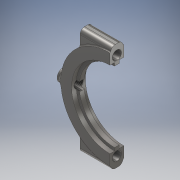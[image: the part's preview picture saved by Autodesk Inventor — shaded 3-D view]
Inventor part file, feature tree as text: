
AUTODESK INVENTOR PART (.ipt)
format: ipt  version: 2017 (Build 210142000, 142)  size: 296,960 bytes
history: native  units: mm
features: extrude x6, sketch x3, fillet x2, plane x2, thread x1, projected_geometry x1
ambient origin geometry x8: Origin, YZ Plane, XZ Plane, XY Plane, X Axis, Y Axis, Z Axis, Center Point
bodies: Body1 (feature_tree)
feature tree (15):
  sketch  "Sketch1"  dims[d0=32.0mm d1=23.0mm d2=0.0mm d3=0.0mm d4=25.0mm d5=0.0mm d6=16.0mm]
  extrude  "Extrusion3"  Depth=16.0mm
  extrude  "Extrusion4"  Depth=1.5mm TaperAngle=0.0deg
  sketch  "Sketch3"  dims[d11=4.5mm d12=0.0mm d13=1.5mm d14=0.0mm]
  extrude  "Extrusion6"  Depth=2.7mm
  extrude  "Extrusion7"  Depth=2.7mm
  fillet  "Fillet1"  [1 undecoded]
  plane  "Work Plane1"
  plane  "Work Plane2"
  sketch  "Sketch4"  dims[d27=3.0mm d42=5.0mm d51=2.7mm d52=2.7mm d53=90.0deg d54=90.0deg d55=90.0deg d56=6.0mm d57=2.75mm d58=1.25mm d59=1.0mm d60=0.0mm d61=24.0mm d62=27.5mm d63=29.0mm d64=1.5mm d65=3.0mm d66=25.75mm d67=0.75mm d68=1.5mm d69=1.5mm d70=24.0mm d71=0.75mm d72=2.75mm d73=1.25mm d74=10.0mm d75=0.0mm d76=10.0mm d77=0.0mm d78=0.5mm d79=6.0mm d84=-22.0mm d85=4.0mm d86=3.0mm d87=3.0mm d88=0.0mm d89=7.5mm d90=0.0mm d91=1.0mm d92=10.0mm d93=0.0mm]
  extrude  "Extrusion8"  TaperAngle=90.0deg  [1 undecoded]
  extrude  "Extrusion9"  TaperAngle=90.0deg  [1 undecoded]
  fillet  "Fillet2"  Radius=6.0mm
  thread  "Thread3"  [1 undecoded]
  projected_geometry  "Projected Loop1"
note: 4 required parameter values undecoded (feature->parameter linkage not recoverable at this tier; creation-order binding heuristic only, values carry confidence <= 0.55)
